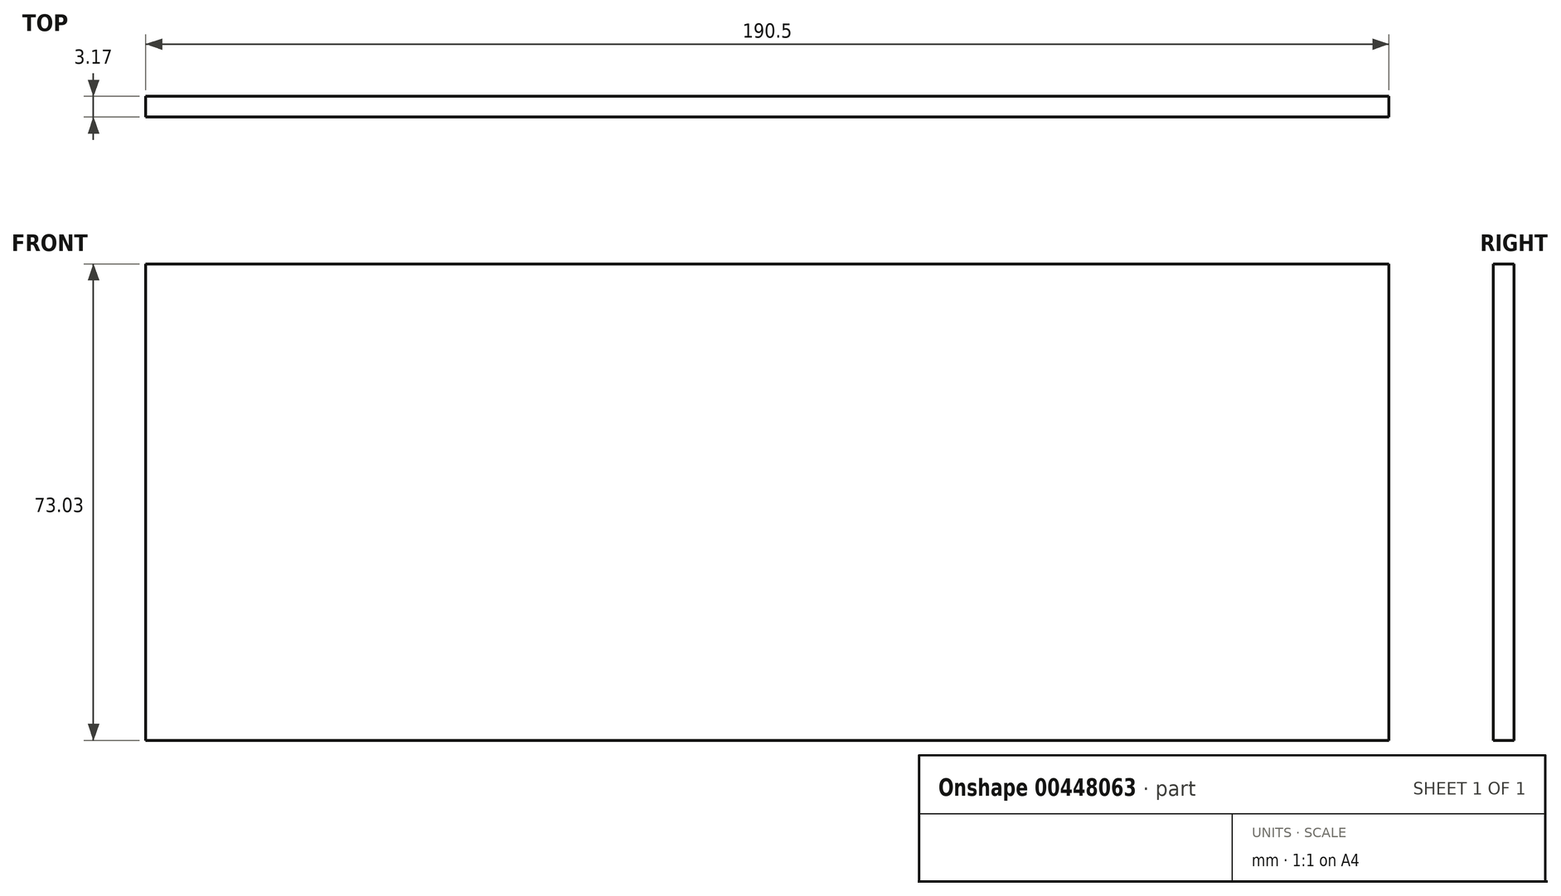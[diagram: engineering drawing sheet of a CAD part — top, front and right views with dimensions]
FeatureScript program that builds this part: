
annotation { "Feature Type Name" : "Feature", "Feature Type Description" : "" }
export const myFeature = defineFeature(function(context is Context, id is Id, definition is map)
    precondition{}
    {
        {
            var Q0;
            Q0=qCreatedBy(makeId("Front.planeOp"),FACE);
            var sketch = newSketch(context, id + "F0", { "sketchPlane" : qUnion([Q0])});
            skLineSegment(sketch, "E0", {"start": v(0, 0) * mm, "end": v(190.5, 0) * mm});
            skLineSegment(sketch, "E1", {"start": v(0, 0) * mm, "end": v(0, 73.02) * mm});
            skLineSegment(sketch, "E2", {"start": v(190.5, 0) * mm, "end": v(190.5, 73.02) * mm});
            skLineSegment(sketch, "E3", {"start": v(0, 73.02) * mm, "end": v(190.5, 73.02) * mm});
            skSolve(sketch);
        }
        {
            var Q0;
            Q0=makeQuery(id+"F0.imprint","IMPRINT",FACE,{"disambiguationData":[TD([[makeQuery(id+"F0.imprint","IMPRINT",EDGE,{"derivedFrom":sQuery(id+"F0.wireOp",EDGE,"E0")}),1.0]])]});
            extrude(context, id + "F1", {"entities" : qUnion([Q0]), "depth" : 3.17 * mm});
        }
    });
